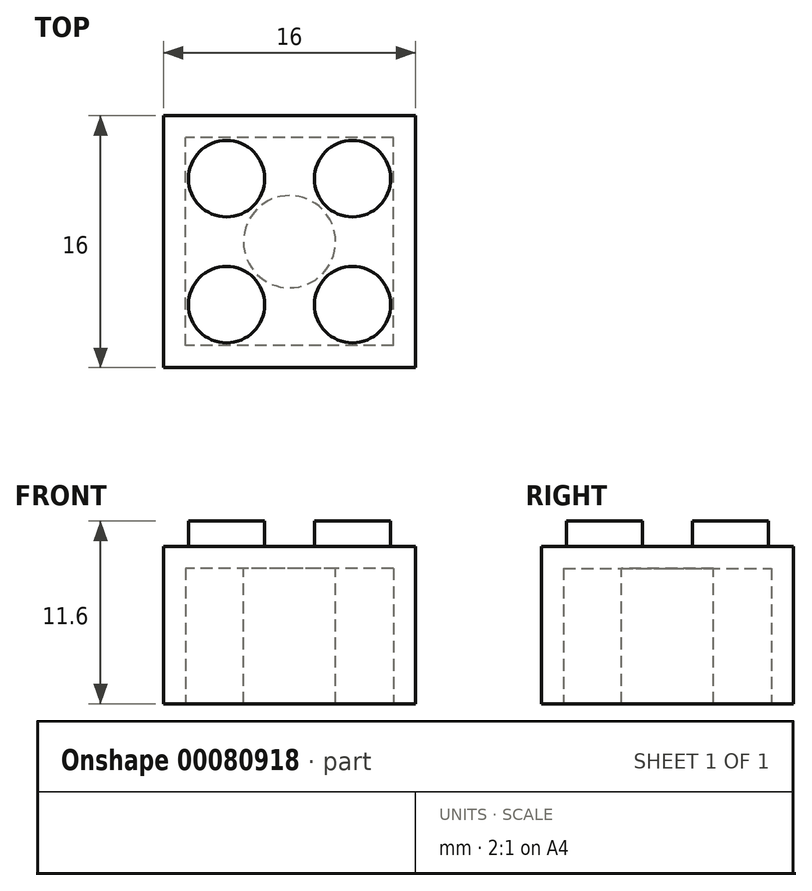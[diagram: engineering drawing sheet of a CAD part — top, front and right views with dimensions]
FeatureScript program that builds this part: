
annotation { "Feature Type Name" : "Feature", "Feature Type Description" : "" }
export const myFeature = defineFeature(function(context is Context, id is Id, definition is map)
    precondition{}
    {
        {
            var Q0;
            Q0=qCreatedBy(makeId("Top.planeOp"),FACE);
            var sketch = newSketch(context, id + "F0", { "sketchPlane" : qUnion([Q0])});
            skLineSegment(sketch, "E0.bottom", {"start": v(8, -8) * mm, "end": v(-8, -8) * mm});
            skLineSegment(sketch, "E0.top", {"start": v(8, 8) * mm, "end": v(-8, 8) * mm});
            skLineSegment(sketch, "E0.left", {"start": v(8, -8) * mm, "end": v(8, 8) * mm});
            skLineSegment(sketch, "E0.right", {"start": v(-8, -8) * mm, "end": v(-8, 8) * mm});
            skPoint(sketch, "E0.middle", {"position": v(0, 0) * mm});
            skSolve(sketch);
        }
        {
            var Q0;
            Q0 = qSketchRegion(id + "F0", true);
            extrude(context, id + "F1", {"entities" : qUnion([Q0]), "depth" : 10 * mm});
        }
        {
            var Q0;
            Q0=makeQuery(id+"F1.opExtrude","CAP_FACE",FACE,{"disambiguationData":[OSD([sQuery(id+"F0.wireOp",EDGE,"E0.bottom"),sQuery(id+"F0.wireOp",EDGE,"E0.top"),sQuery(id+"F0.wireOp",EDGE,"E0.left"),sQuery(id+"F0.wireOp",EDGE,"E0.right")])],"isStart":true});
            shell(context, id + "F2", {"entities" : qUnion([Q0]), "thickness" : 1.4 * mm});
        }
        {
            var Q0;
            Q0=makeQuery(id+"F1.opExtrude","CAP_FACE",FACE,{"disambiguationData":[OSD([sQuery(id+"F0.wireOp",EDGE,"E0.bottom"),sQuery(id+"F0.wireOp",EDGE,"E0.top"),sQuery(id+"F0.wireOp",EDGE,"E0.left"),sQuery(id+"F0.wireOp",EDGE,"E0.right")])],"isStart":false});
            var sketch = newSketch(context, id + "F3", { "sketchPlane" : qUnion([Q0])});
            skCircle(sketch, "E1", {"center": v(-4, -4) * mm, "radius": 2.43 * mm});
            skCircle(sketch, "E2.0.1.0", {"center": v(-4, 4) * mm, "radius": 2.43 * mm});
            skCircle(sketch, "E2.1.0.0", {"center": v(4, -4) * mm, "radius": 2.43 * mm});
            skCircle(sketch, "E2.1.1.0", {"center": v(4, 4) * mm, "radius": 2.43 * mm});
            skLineSegment(sketch, "E2.direction1", {"start": v(-4, -4) * mm, "end": v(4, -4) * mm, "construction": true});
            skLineSegment(sketch, "E2.direction2", {"start": v(-4, -4) * mm, "end": v(-4, 4) * mm, "construction": true});
            skSolve(sketch);
        }
        {
            var Q0;
            Q0 = qSketchRegion(id + "F3", true);
            extrude(context, id + "F4", {"entities" : qUnion([Q0]), "operationType" : NewBodyOperationType.ADD, "depth" : 1.6 * mm});
        }
        {
            var Q0;
            Q0=makeQuery(id+"F1.opExtrude","CAP_FACE",FACE,{"disambiguationData":[OSD([sQuery(id+"F0.wireOp",EDGE,"E0.bottom"),sQuery(id+"F0.wireOp",EDGE,"E0.top"),sQuery(id+"F0.wireOp",EDGE,"E0.left"),sQuery(id+"F0.wireOp",EDGE,"E0.right")])],"isStart":false});
            var sketch = newSketch(context, id + "F5", { "sketchPlane" : qUnion([Q0])});
            skCircle(sketch, "E3", {"center": v(0, 0) * mm, "radius": 2.93 * mm});
            skSolve(sketch);
        }
        {
            var Q0;
            Q0 = qSketchRegion(id + "F5", true);
            extrude(context, id + "F6", {"entities" : qUnion([Q0]), "operationType" : NewBodyOperationType.ADD, "oppositeDirection" : true, "depth" : 10 * mm});
        }
    });
